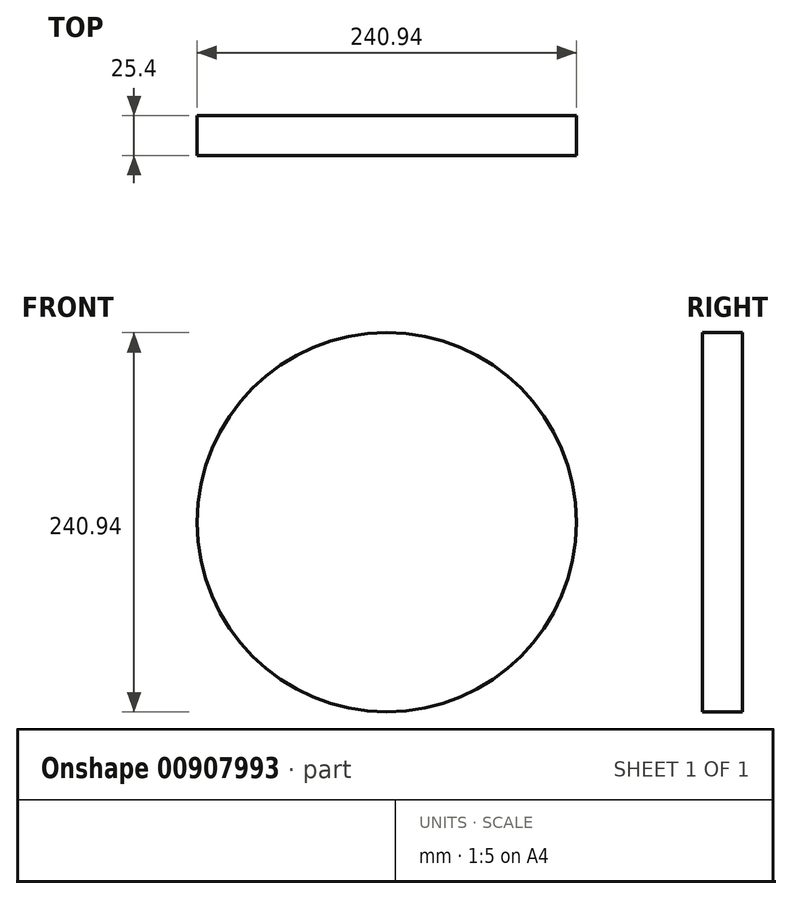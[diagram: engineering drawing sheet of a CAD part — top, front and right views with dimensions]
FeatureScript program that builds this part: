
annotation { "Feature Type Name" : "Feature", "Feature Type Description" : "" }
export const myFeature = defineFeature(function(context is Context, id is Id, definition is map)
    precondition{}
    {
        {
            var Q0;
            Q0=qCreatedBy(makeId("Front.planeOp"),FACE);
            var sketch = newSketch(context, id + "F0", { "sketchPlane" : qUnion([Q0])});
            skCircle(sketch, "E0", {"center": v(0, 0) * mm, "radius": 120.47 * mm});
            skSolve(sketch);
        }
        {
            var Q0;
            Q0 = qSketchRegion(id + "F0", true);
            extrude(context, id + "F1", {"entities" : qUnion([Q0]), "depth" : 25.4 * mm, "offsetDistance" : 25.4 * mm});
        }
    });
